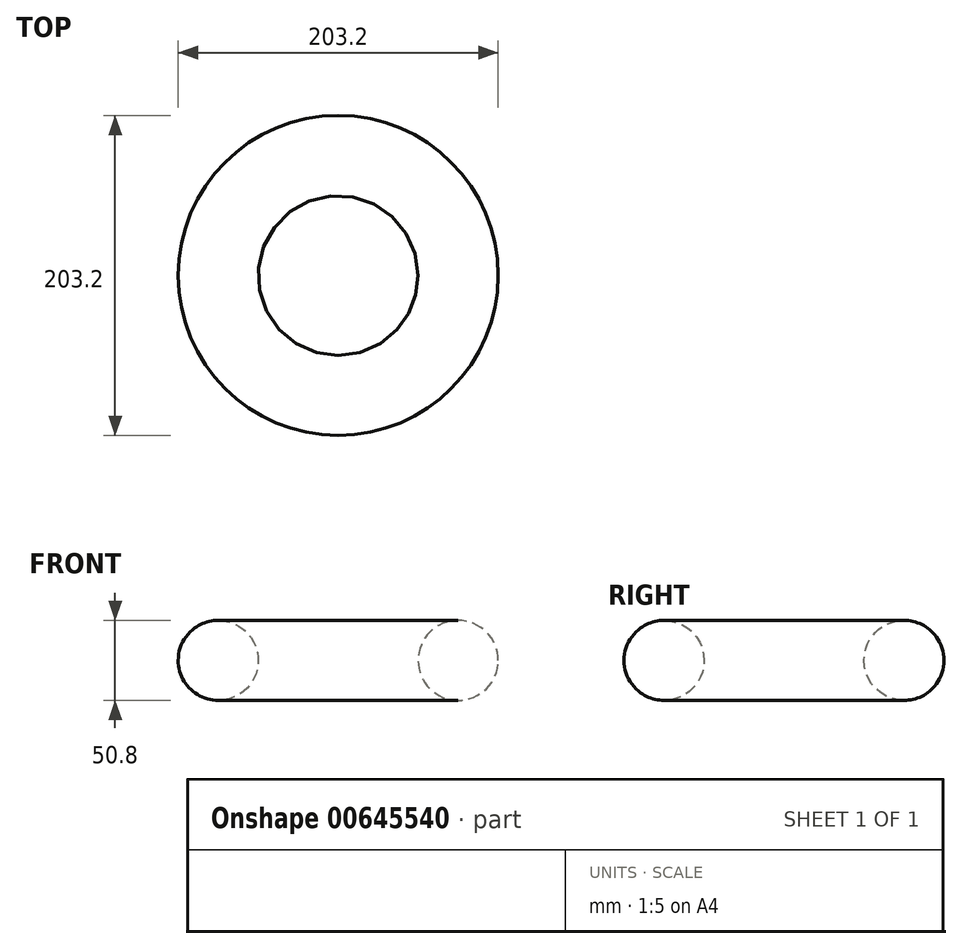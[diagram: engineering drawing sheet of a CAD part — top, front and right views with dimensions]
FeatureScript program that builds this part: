
annotation { "Feature Type Name" : "Feature", "Feature Type Description" : "" }
export const myFeature = defineFeature(function(context is Context, id is Id, definition is map)
    precondition{}
    {
        {
            var Q0;
            Q0=qCreatedBy(makeId("Front.planeOp"),FACE);
            var sketch = newSketch(context, id + "F0", { "sketchPlane" : qUnion([Q0])});
            skCircle(sketch, "E0", {"center": v(76.2, 0) * mm, "radius": 25.4 * mm});
            skLineSegment(sketch, "E1", {"start": v(0, 68.45) * mm, "end": v(0, -42.36) * mm, "construction": true});
            skSolve(sketch);
        }
        {
            var Q0;
            Q0=makeQuery(id+"F0.imprint","IMPRINT",FACE,{"disambiguationData":[TD([[makeQuery(id+"F0.imprint","IMPRINT",EDGE,{"derivedFrom":sQuery(id+"F0.wireOp",EDGE,"E0")}),1.0]])]});
            var Q1;
            Q1=sQuery(id+"F0.wireOp",EDGE,"E1");
            revolve(context, id + "F1", {"entities" : qUnion([Q0]), "axis" : qUnion([Q1]), "revolveType" : RevolveType.FULL});
        }
    });
